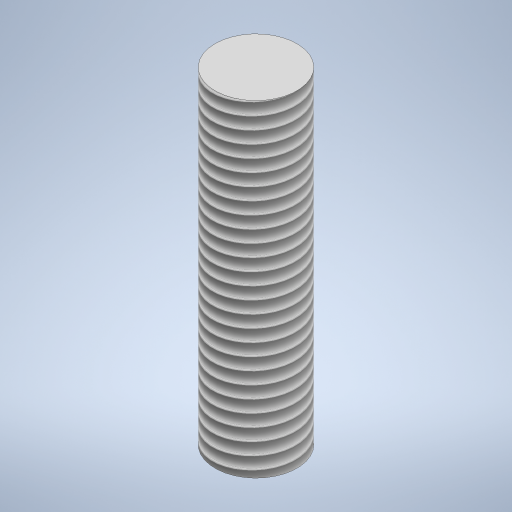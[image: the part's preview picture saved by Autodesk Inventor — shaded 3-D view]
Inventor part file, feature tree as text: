
AUTODESK INVENTOR PART (.ipt)
format: ipt  version: 2023 (Build 270158000, 158)  size: 289,792 bytes
history: native  units: mm
features: other x1, extrude x1, thread x1, sketch x1
ambient origin geometry x8: Origin, YZ Plane, XZ Plane, XY Plane, X Axis, Y Axis, Z Axis, Center Point
bodies: Body1 (feature_tree)
feature tree (4):
  other  "Твердое тело1"
  extrude  "Выдавливание1"  Depth=10.0mm
  thread  "Резьба1"
  sketch  "Эскиз1"
